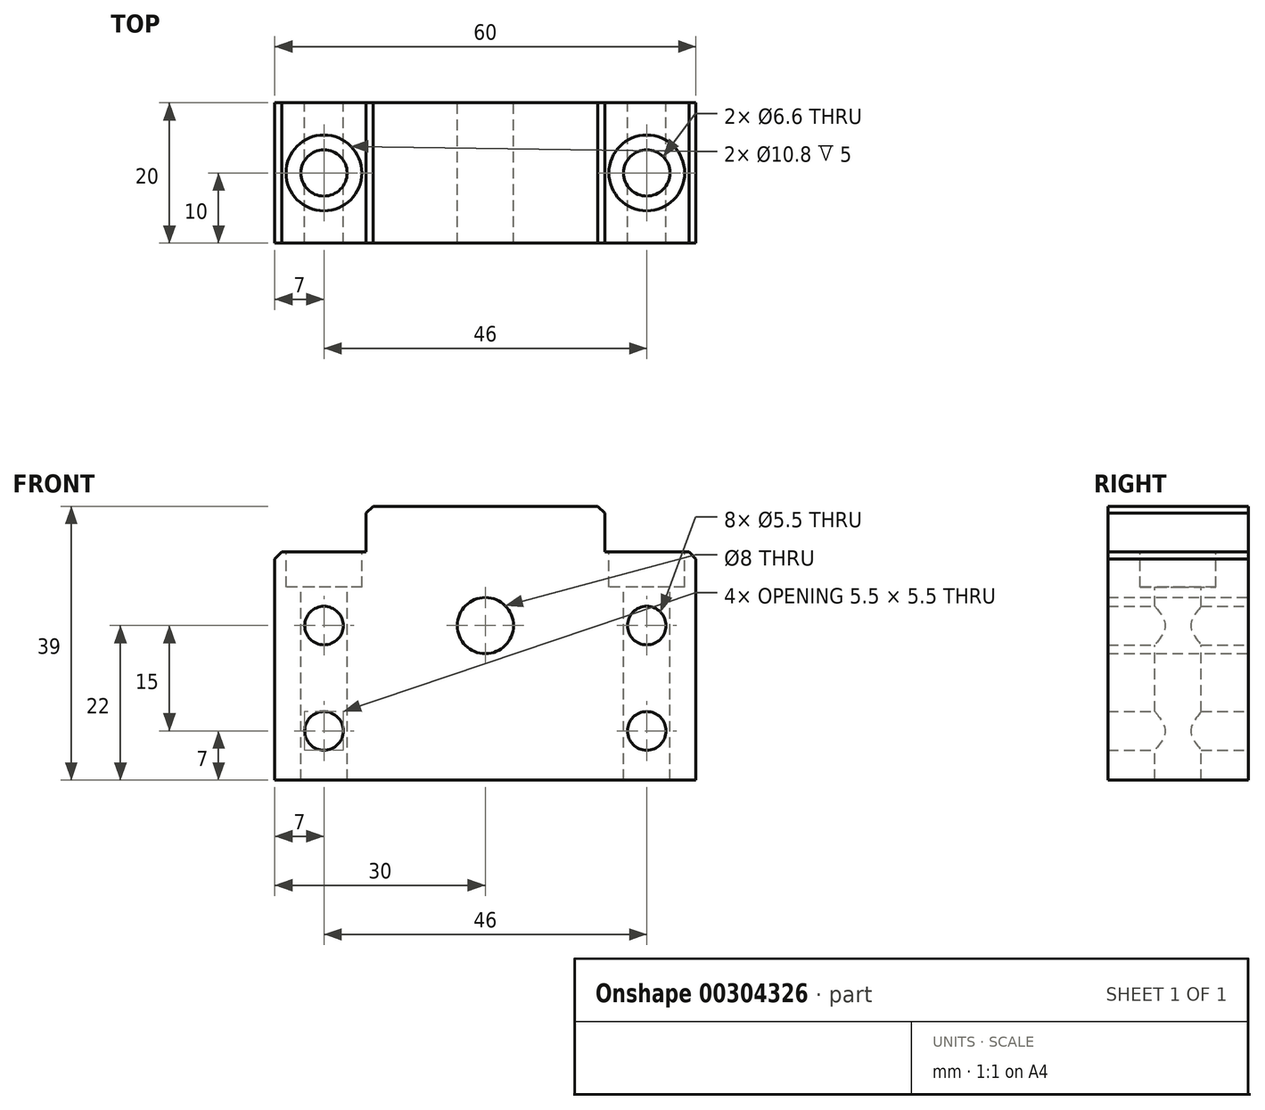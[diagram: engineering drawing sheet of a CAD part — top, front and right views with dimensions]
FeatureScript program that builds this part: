
annotation { "Feature Type Name" : "Feature", "Feature Type Description" : "" }
export const myFeature = defineFeature(function(context is Context, id is Id, definition is map)
    precondition{}
    {
        {
            var Q0;
            Q0=qCreatedBy(makeId("Front.planeOp"),FACE);
            var sketch = newSketch(context, id + "F0", { "sketchPlane" : qUnion([Q0])});
            skCircle(sketch, "E0", {"center": v(0, 0) * mm, "radius": 12.5 * mm, "construction": true});
            skLineSegment(sketch, "E1.bottom", {"start": v(-17, 17) * mm, "end": v(17, 17) * mm});
            skLineSegment(sketch, "E1.left", {"start": v(-17, 17) * mm, "end": v(-17, 10.5) * mm});
            skLineSegment(sketch, "E1.right", {"start": v(17, 17) * mm, "end": v(17, 10.5) * mm});
            skLineSegment(sketch, "E2.bottom", {"start": v(-30, 10.5) * mm, "end": v(-17, 10.5) * mm});
            skLineSegment(sketch, "E2.top", {"start": v(-30, -22) * mm, "end": v(30, -22) * mm});
            skLineSegment(sketch, "E2.left", {"start": v(-30, 10.5) * mm, "end": v(-30, -22) * mm});
            skLineSegment(sketch, "E2.right", {"start": v(30, 10.5) * mm, "end": v(30, -22) * mm});
            skLineSegment(sketch, "E3", {"start": v(-23, 10.5) * mm, "end": v(-23, -22) * mm, "construction": true});
            skLineSegment(sketch, "E4", {"start": v(23, 10.5) * mm, "end": v(23, -22) * mm, "construction": true});
            skLineSegment(sketch, "E5", {"start": v(-30, 0) * mm, "end": v(30, 0) * mm, "construction": true});
            skLineSegment(sketch, "E6", {"start": v(-30, -15) * mm, "end": v(30, -15) * mm, "construction": true});
            skLineSegment(sketch, "E7.trimOffspring", {"start": v(17, 10.5) * mm, "end": v(30, 10.5) * mm});
            skLineSegment(sketch, "E8", {"start": v(0, 17) * mm, "end": v(0, -22) * mm, "construction": true});
            skLineSegment(sketch, "E9", {"start": v(0, 0) * mm, "end": v(13.6, 0) * mm, "construction": true});
            skCircle(sketch, "E10", {"center": v(0, 0) * mm, "radius": 4 * mm});
            skCircle(sketch, "E11", {"center": v(-23, 0) * mm, "radius": 2.75 * mm});
            skCircle(sketch, "E12", {"center": v(-23, -15) * mm, "radius": 2.75 * mm});
            skCircle(sketch, "E13", {"center": v(23, -15) * mm, "radius": 2.75 * mm});
            skCircle(sketch, "E14", {"center": v(23, 0) * mm, "radius": 2.75 * mm});
            skSolve(sketch);
        }
        {
            var Q0;
            Q0=makeQuery(id+"F0.imprint","IMPRINT",FACE,{"disambiguationData":[TD([[makeQuery(id+"F0.imprint","IMPRINT",EDGE,{"derivedFrom":sQuery(id+"F0.wireOp",EDGE,"E1.bottom")}),-1.0]])]});
            extrude(context, id + "F1", {"entities" : qUnion([Q0]), "depth" : 20 * mm});
        }
        {
            var Q0;
            Q0=makeQuery(id+"F1.opExtrude","SWEPT_EDGE",EDGE,{"disambiguationData":[OSD([sQuery(id+"F0.wireOp",EDGE,"E1.bottom"),sQuery(id+"F0.wireOp",EDGE,"E1.right")])]});
            var Q1;
            Q1=makeQuery(id+"F1.opExtrude","SWEPT_EDGE",EDGE,{"disambiguationData":[OSD([sQuery(id+"F0.wireOp",EDGE,"E1.bottom"),sQuery(id+"F0.wireOp",EDGE,"E1.left")])]});
            var Q2;
            Q2=makeQuery(id+"F1.opExtrude","SWEPT_EDGE",EDGE,{"disambiguationData":[OSD([sQuery(id+"F0.wireOp",EDGE,"E2.right"),sQuery(id+"F0.wireOp",EDGE,"E7.trimOffspring")])]});
            var Q3;
            Q3=makeQuery(id+"F1.opExtrude","SWEPT_EDGE",EDGE,{"disambiguationData":[OSD([sQuery(id+"F0.wireOp",EDGE,"E2.bottom"),sQuery(id+"F0.wireOp",EDGE,"E2.left")])]});
            chamfer(context, id + "F2", {"entities" : qUnion([Q0, Q1, Q2, Q3]), "width" : 1 * mm, "tangentPropagation" : true});
        }
        {
            var Q0;
            Q0=makeQuery(id+"F1.opExtrude","SWEPT_FACE",FACE,{"disambiguationData":[OSD([sQuery(id+"F0.wireOp",EDGE,"E7.trimOffspring")])]});
            var sketch = newSketch(context, id + "F3", { "sketchPlane" : qUnion([Q0])});
            skLineSegment(sketch, "E15", {"start": v(29, -10) * mm, "end": v(-29, -10) * mm, "construction": true});
            skPoint(sketch, "E16", {"position": v(-23, -10) * mm});
            skPoint(sketch, "E17", {"position": v(23, -10) * mm});
            skLineSegment(sketch, "E18", {"start": v(0, -10) * mm, "end": v(0, -4.95) * mm, "construction": true});
            skPoint(sketch, "E18.endSnap0", {"position": v(0, -10) * mm});
            skSolve(sketch);
        }
        {
            var Q0;
            Q0=sQuery(id+"F3.wireOp",VERTEX,"E16");
            var Q1;
            Q1=sQuery(id+"F3.wireOp",VERTEX,"E17");
            var Q2;
            Q2=makeQuery(id+"F1.opExtrude","SWEPT_BODY",BODY,{"disambiguationData":[OSD([sQuery(id+"F0.wireOp",EDGE,"E1.bottom"),sQuery(id+"F0.wireOp",EDGE,"E1.left"),sQuery(id+"F0.wireOp",EDGE,"E1.right"),sQuery(id+"F0.wireOp",EDGE,"E2.bottom"),sQuery(id+"F0.wireOp",EDGE,"E2.top"),sQuery(id+"F0.wireOp",EDGE,"E2.left"),sQuery(id+"F0.wireOp",EDGE,"E2.right"),sQuery(id+"F0.wireOp",EDGE,"E7.trimOffspring"),sQuery(id+"F0.wireOp",EDGE,"E10"),sQuery(id+"F0.wireOp",EDGE,"E11"),sQuery(id+"F0.wireOp",EDGE,"E12"),sQuery(id+"F0.wireOp",EDGE,"E13"),sQuery(id+"F0.wireOp",EDGE,"E14")])]});
            hole(context, id + "F4", {"style" : HoleStyle.C_BORE, "endStyle" : HoleEndStyle.THROUGH, "standardTappedOrClearance" : lookupTablePath({ "standard" : "ISO", "size" : "6.6", "type" : "Drilled" }), "standardBlindInLast" : lookupTablePath({ "standard" : "ISO", "size" : "6.6", "type" : "Drilled" }), "holeDiameter" : 6.6 * mm, "cBoreDiameter" : 10.8 * mm, "cBoreDepth" : 5 * mm, "tappedDepth" : 8 * mm, "tapClearance" : 3, "locations" : qUnion([Q0, Q1]), "scope" : qUnion([Q2])});
        }
    });
